# Revit family: Módulo de Comando Endereçável Cygnus MSC-G ILUMAC
name_source: partatom
category: Dispositivos de alarme de incêndio
units: mm (PartAtom-declared; Revit-internal decimal feet)

## family parameters
Com base no plano de trabalho = Não
Compartilhado = Não
Corte com vazios quando carregada = Não
Cota do conector redondo = Utilizar diâmetro
Manter orientação da anotação = Não
Número OmniClass = 23.80.30.11.17
Ponto de cálculo do ambiente = Não
Sempre na vertical = Sim
Tipo de parte = Normal
Título OmniClass = Distribution Boards and Control Panels

## types (1)
- MSC-G
    Acionamento = Em pré-alarme (não respeita retardo do sistema)
Em alarme (respeita retardo do sistema)
Possui trimpot para retardo externo ao sistema
    Consumo = 1,5mA em supervisão | 2mA em alarme
    Consumo da fonte auxiliar ou V+ = 60mA em alarme sem dispositivo*
    Código do Produto = 007051
    Descrição = Módulo de Comando Endereçável Cygnus MSC-G
    Dimensões (AxLxP) = 90x90x55mm
    Elevação padrão = 0 mm  [stored 0 ft]
    Endereços programáveis = 001 à 125 (por laço)
    Endereços utilizados = 1 endereço
    Fabricante = ILUMAC
    Fixação = Sobrepor c/ entrada superior/inferior para tubo 3/4"
    Grau de proteção = IP42 (à prova de respingo d’água)
    Limitação Saída de Contato Seco = Tensão máx 30V / 1A (carga resistiva)
    Limitação Saída para Sirene = 900mA @ 28Vcc
    Material da caixa = Caixa plástica ABS na cor branco
    Modelo = MSC-G
    Normas técnicas aplicáveis = NBR 17240 / ISO 7240-18
    Peso = 145g
    Protocolo de comunicação = CYGNUS (proprietário)
    Resistor de final de linha (RFL) = 10KΩ - monitora a saída para sirenes
    Secção máxima do cabo = 2,5mm²
    Temperatura de operação = 0 à 50oC
    Tensão de operação = 20 a 30Vcc
    Tensão nominal = 24Vcc
    Tipo de saída = 1 saída contato seco SPDT-NA
1 saída para sirenes convencionais
1 saída contato seco pulso SPDT-NF
    Umidade relativa = 0 à 95% (sem condensação)

note: [stored X ft] marks values corroborated as IEEE doubles in the binary element streams (Revit-internal decimal feet)
